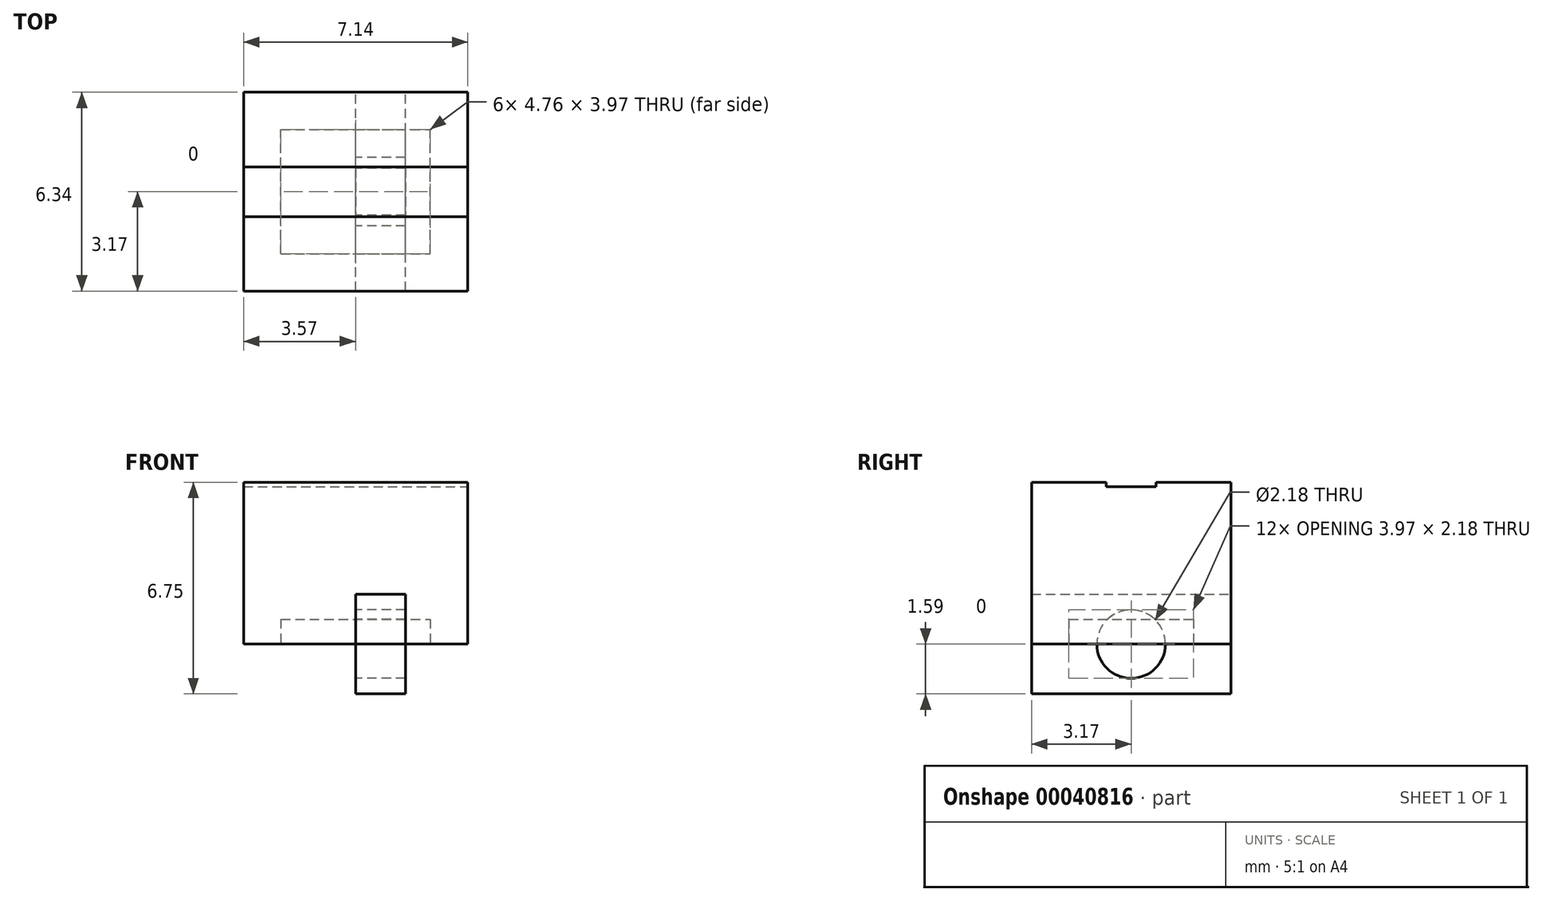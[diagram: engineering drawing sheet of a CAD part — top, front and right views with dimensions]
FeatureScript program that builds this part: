
annotation { "Feature Type Name" : "Feature", "Feature Type Description" : "" }
export const myFeature = defineFeature(function(context is Context, id is Id, definition is map)
    precondition{}
    {
        {
            var Q0;
            Q0=qCreatedBy(makeId("Top.planeOp"),FACE);
            var sketch = newSketch(context, id + "F0", { "sketchPlane" : qUnion([Q0])});
            skLineSegment(sketch, "E0.rect.bottom", {"start": v(-3.57, 3.17) * mm, "end": v(3.57, 3.17) * mm});
            skLineSegment(sketch, "E0.rect.top", {"start": v(-3.57, -3.18) * mm, "end": v(3.57, -3.18) * mm});
            skLineSegment(sketch, "E0.rect.left", {"start": v(-3.57, 3.17) * mm, "end": v(-3.57, -3.18) * mm});
            skLineSegment(sketch, "E0.rect.right", {"start": v(3.57, 3.18) * mm, "end": v(3.57, -3.18) * mm});
            skPoint(sketch, "E0.rect.middle", {"position": v(0, 0) * mm});
            skSolve(sketch);
        }
        {
            var Q0;
            Q0 = qSketchRegion(id + "F0", true);
            extrude(context, id + "F1", {"entities" : qUnion([Q0]), "depth" : 5.16 * mm});
        }
        {
            var Q0;
            Q0=makeQuery(id+"F1.opExtrude","CAP_FACE",FACE,{"disambiguationData":[OSD([sQuery(id+"F0.wireOp",EDGE,"E0.rect.bottom"),sQuery(id+"F0.wireOp",EDGE,"E0.rect.top"),sQuery(id+"F0.wireOp",EDGE,"E0.rect.left"),sQuery(id+"F0.wireOp",EDGE,"E0.rect.right")])],"isStart":true});
            var sketch = newSketch(context, id + "F2", { "sketchPlane" : qUnion([Q0])});
            skLineSegment(sketch, "E1.rect.bottom", {"start": v(-2.38, 1.98) * mm, "end": v(2.38, 1.98) * mm});
            skLineSegment(sketch, "E1.rect.top", {"start": v(-2.38, -1.98) * mm, "end": v(2.38, -1.98) * mm});
            skLineSegment(sketch, "E1.rect.left", {"start": v(-2.38, 1.98) * mm, "end": v(-2.38, -1.98) * mm});
            skLineSegment(sketch, "E1.rect.right", {"start": v(2.38, 1.98) * mm, "end": v(2.38, -1.98) * mm});
            skPoint(sketch, "E1.rect.middle", {"position": v(0, 0) * mm});
            skSolve(sketch);
        }
        {
            var Q0;
            Q0 = qSketchRegion(id + "F2", true);
            extrude(context, id + "F3", {"entities" : qUnion([Q0]), "operationType" : NewBodyOperationType.REMOVE, "oppositeDirection" : true, "depth" : 0.8 * mm});
        }
        {
            var Q0;
            Q0=makeQuery(id+"F1.opExtrude","CAP_FACE",FACE,{"disambiguationData":[OSD([sQuery(id+"F0.wireOp",EDGE,"E0.rect.bottom"),sQuery(id+"F0.wireOp",EDGE,"E0.rect.top"),sQuery(id+"F0.wireOp",EDGE,"E0.rect.left"),sQuery(id+"F0.wireOp",EDGE,"E0.rect.right")])],"isStart":false});
            var sketch = newSketch(context, id + "F4", { "sketchPlane" : qUnion([Q0])});
            skLineSegment(sketch, "E2.rect.bottom", {"start": v(-9.21, 0.8) * mm, "end": v(9.21, 0.8) * mm});
            skLineSegment(sketch, "E2.rect.top", {"start": v(-9.21, -0.8) * mm, "end": v(9.21, -0.8) * mm});
            skLineSegment(sketch, "E2.rect.left", {"start": v(-9.21, 0.8) * mm, "end": v(-9.21, -0.8) * mm});
            skLineSegment(sketch, "E2.rect.right", {"start": v(9.21, 0.8) * mm, "end": v(9.21, -0.8) * mm});
            skPoint(sketch, "E2.rect.middle", {"position": v(0, 0) * mm});
            skSolve(sketch);
        }
        {
            var Q0;
            Q0 = qSketchRegion(id + "F4", true);
            extrude(context, id + "F5", {"entities" : qUnion([Q0]), "operationType" : NewBodyOperationType.REMOVE, "oppositeDirection" : true, "depth" : ((13 / 64) - (1 / 16)) * mm});
        }
        {
            var Q0;
            {var subQ0=sQuery(id+"F0.wireOp",EDGE,"E0.rect.bottom");var subQ1=sQuery(id+"F0.wireOp",EDGE,"E0.rect.left");var subQ2=sQuery(id+"F0.wireOp",EDGE,"E0.rect.right");Q0=makeQuery(id+"F5.boolean.opBoolean","SPLIT",FACE,{"disambiguationData":[TD([makeQuery(id+"F1.opExtrude","SWEPT_FACE",FACE,{"disambiguationData":[OSD([subQ0])]})])],"derivedFrom":makeQuery(id+"F1.opExtrude","CAP_FACE",FACE,{"disambiguationData":[OSD([subQ0,sQuery(id+"F0.wireOp",EDGE,"E0.rect.top"),subQ1,subQ2])],"isStart":false})});}
            cPlane(context, id + "F6", {"entities" : qUnion([Q0]), "cplaneType" : CPlaneType.OFFSET, "offset" : 0 * mm, "width" : 152.4 * mm, "height" : 152.4 * mm});
        }
        {
            var Q0;
            Q0=qCreatedBy(id+"F6.planeOp",FACE);
            var sketch = newSketch(context, id + "F7", { "sketchPlane" : qUnion([Q0])});
            skLineSegment(sketch, "E3.rect.bottom", {"start": v(-1.14, 4.45) * mm, "end": v(1.14, 4.45) * mm});
            skLineSegment(sketch, "E3.rect.top", {"start": v(-1.14, -4.45) * mm, "end": v(1.14, -4.45) * mm});
            skLineSegment(sketch, "E3.rect.left", {"start": v(-1.14, 4.45) * mm, "end": v(-1.14, -4.45) * mm});
            skLineSegment(sketch, "E3.rect.right", {"start": v(1.14, 4.45) * mm, "end": v(1.14, -4.45) * mm});
            skPoint(sketch, "E3.rect.middle", {"position": v(0, 0) * mm});
            skSolve(sketch);
        }
        {
            var Q0;
            Q0 = qSketchRegion(id + "F7", true);
            extrude(context, id + "F8", {"entities" : qUnion([Q0]), "operationType" : NewBodyOperationType.REMOVE, "oppositeDirection" : true, "depth" : ((13 / 64) - .7) * mm});
        }
        {
            var Q0;
            Q0=qCreatedBy(makeId("Right.planeOp"),FACE);
            var sketch = newSketch(context, id + "F9", { "sketchPlane" : qUnion([Q0])});
            skLineSegment(sketch, "E4.rect.bottom", {"start": v(-3.18, 1.59) * mm, "end": v(3.18, 1.59) * mm});
            skLineSegment(sketch, "E4.rect.top", {"start": v(-3.18, -1.59) * mm, "end": v(3.18, -1.59) * mm});
            skLineSegment(sketch, "E4.rect.left", {"start": v(-3.17, 1.59) * mm, "end": v(-3.18, -1.59) * mm});
            skLineSegment(sketch, "E4.rect.right", {"start": v(3.18, 1.59) * mm, "end": v(3.18, -1.59) * mm});
            skPoint(sketch, "E4.rect.middle", {"position": v(0, 0) * mm});
            skCircle(sketch, "E5", {"center": v(0, 0) * mm, "radius": 1.1 * mm});
            skSolve(sketch);
        }
        {
            var Q0;
            Q0=makeQuery(id+"F9.imprint","IMPRINT",FACE,{"disambiguationData":[TD([[makeQuery(id+"F9.imprint","IMPRINT",EDGE,{"derivedFrom":sQuery(id+"F9.wireOp",EDGE,"E4.rect.bottom")}),-1.0]])]});
            extrude(context, id + "F10", {"entities" : qUnion([Q0]), "depth" : 1.59 * mm});
        }
    });
